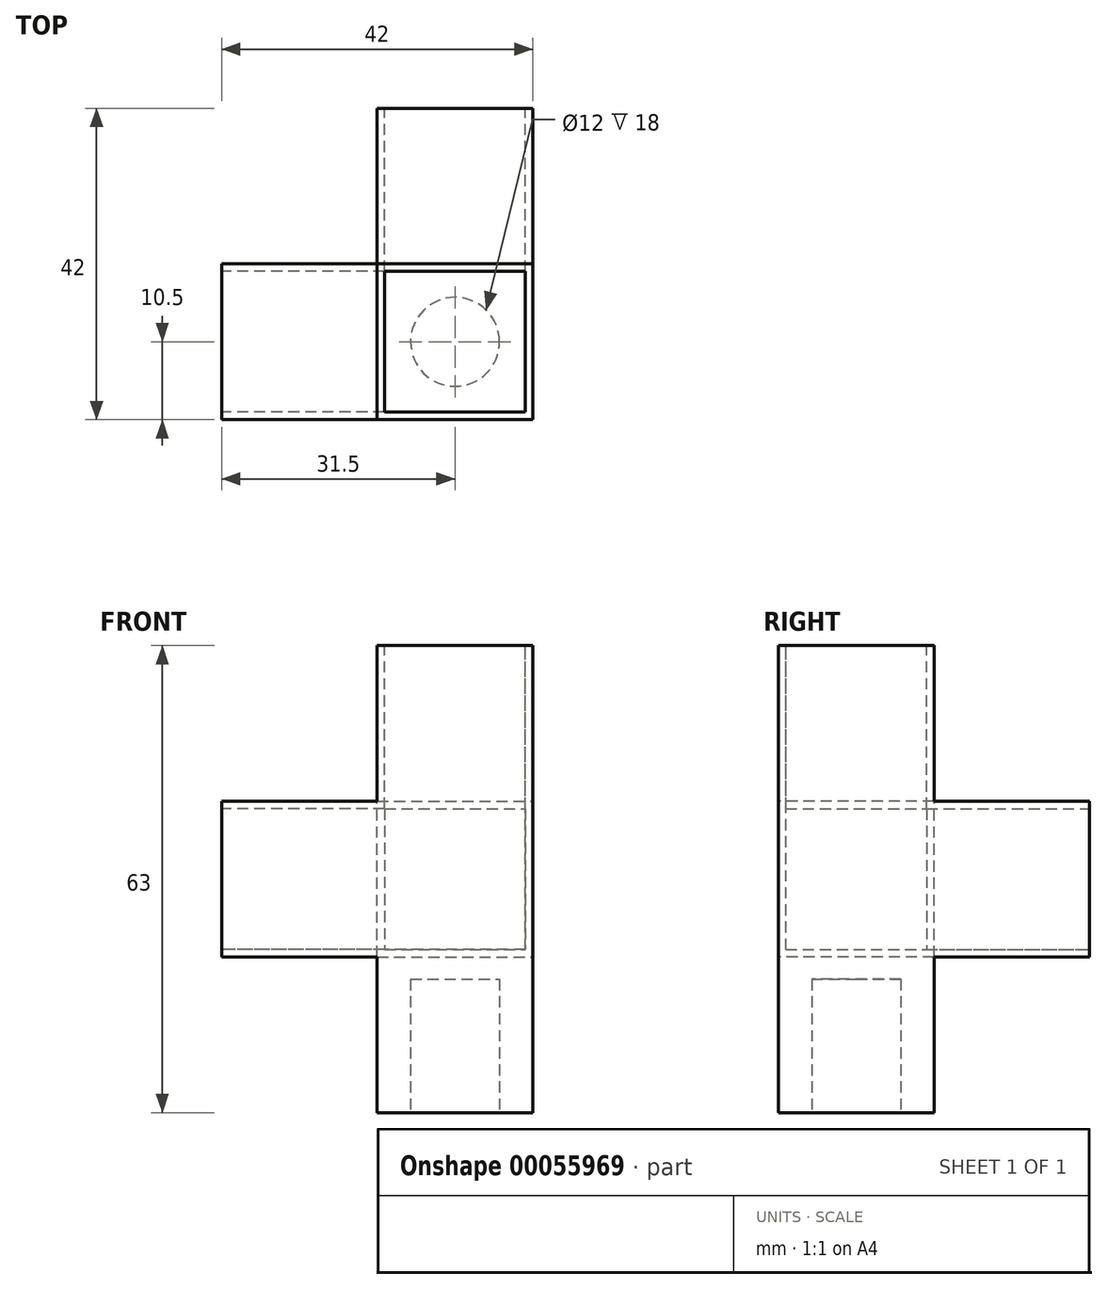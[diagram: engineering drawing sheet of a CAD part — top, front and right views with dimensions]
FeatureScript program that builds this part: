
annotation { "Feature Type Name" : "Feature", "Feature Type Description" : "" }
export const myFeature = defineFeature(function(context is Context, id is Id, definition is map)
    precondition{}
    {
        {
            var Q0;
            Q0=qCreatedBy(makeId("Top.planeOp"),FACE);
            var sketch = newSketch(context, id + "F0", { "sketchPlane" : qUnion([Q0])});
            skLineSegment(sketch, "E0.rect.bottom", {"start": v(21, 21) * mm, "end": v(-21, 21) * mm});
            skLineSegment(sketch, "E0.rect.top", {"start": v(21, -21) * mm, "end": v(-21, -21) * mm});
            skLineSegment(sketch, "E0.rect.left", {"start": v(21, 21) * mm, "end": v(21, -21) * mm});
            skLineSegment(sketch, "E0.rect.right", {"start": v(-21, 21) * mm, "end": v(-21, -21) * mm});
            skPoint(sketch, "E0.rect.middle", {"position": v(0, 0) * mm});
            skSolve(sketch);
        }
        {
            var Q0;
            Q0=makeQuery(id+"F0.imprint","IMPRINT",FACE,{"disambiguationData":[TD([[makeQuery(id+"F0.imprint","IMPRINT",EDGE,{"derivedFrom":sQuery(id+"F0.wireOp",EDGE,"E0.rect.bottom")}),1.0]])]});
            extrude(context, id + "F1", {"entities" : qUnion([Q0]), "depth" : 42 * mm});
        }
        {
            var Q0;
            Q0=makeQuery(id+"F1.opExtrude","CAP_FACE",FACE,{"disambiguationData":[OSD([sQuery(id+"F0.wireOp",EDGE,"E0.rect.bottom"),sQuery(id+"F0.wireOp",EDGE,"E0.rect.top"),sQuery(id+"F0.wireOp",EDGE,"E0.rect.left"),sQuery(id+"F0.wireOp",EDGE,"E0.rect.right")])],"isStart":false});
            var sketch = newSketch(context, id + "F2", { "sketchPlane" : qUnion([Q0])});
            skLineSegment(sketch, "E1.bottom", {"start": v(-21, 21) * mm, "end": v(0, 21) * mm});
            skLineSegment(sketch, "E1.top", {"start": v(-21, 0) * mm, "end": v(0, 0) * mm});
            skLineSegment(sketch, "E1.left", {"start": v(-21, 21) * mm, "end": v(-21, 0) * mm});
            skLineSegment(sketch, "E1.right", {"start": v(0, 21) * mm, "end": v(0, 0) * mm});
            skSolve(sketch);
        }
        {
            var Q0;
            Q0=makeQuery(id+"F2.imprint","IMPRINT",FACE,{"disambiguationData":[TD([[makeQuery(id+"F2.imprint","IMPRINT",EDGE,{"derivedFrom":sQuery(id+"F2.wireOp",EDGE,"E1.bottom")}),1.0]])]});
            extrude(context, id + "F3", {"entities" : qUnion([Q0]), "operationType" : NewBodyOperationType.REMOVE, "endBound" : BoundingType.UP_TO_NEXT, "oppositeDirection" : true, "depth" : 25 * mm});
        }
        {
            var Q0;
            Q0=makeQuery(id+"F1.opExtrude","SWEPT_FACE",FACE,{"disambiguationData":[OSD([sQuery(id+"F0.wireOp",EDGE,"E0.rect.top")])]});
            var sketch = newSketch(context, id + "F4", { "sketchPlane" : qUnion([Q0])});
            skLineSegment(sketch, "E2.bottom", {"start": v(-21, 42) * mm, "end": v(0, 42) * mm});
            skLineSegment(sketch, "E2.top", {"start": v(-21, 21) * mm, "end": v(0, 21) * mm});
            skLineSegment(sketch, "E2.left", {"start": v(-21, 42) * mm, "end": v(-21, 21) * mm});
            skLineSegment(sketch, "E2.right", {"start": v(0, 42) * mm, "end": v(0, 21) * mm});
            skSolve(sketch);
        }
        {
            var Q0;
            Q0=makeQuery(id+"F4.imprint","IMPRINT",FACE,{"disambiguationData":[TD([[makeQuery(id+"F4.imprint","IMPRINT",EDGE,{"derivedFrom":sQuery(id+"F4.wireOp",EDGE,"E2.bottom")}),1.0]])]});
            extrude(context, id + "F5", {"entities" : qUnion([Q0]), "operationType" : NewBodyOperationType.REMOVE, "endBound" : BoundingType.UP_TO_NEXT, "oppositeDirection" : true, "depth" : 25 * mm});
        }
        {
            var Q0;
            Q0=makeQuery(id+"F1.opExtrude","SWEPT_FACE",FACE,{"disambiguationData":[OSD([sQuery(id+"F0.wireOp",EDGE,"E0.rect.left")])]});
            var sketch = newSketch(context, id + "F6", { "sketchPlane" : qUnion([Q0])});
            skLineSegment(sketch, "E3.bottom", {"start": v(21, 42) * mm, "end": v(0, 42) * mm});
            skLineSegment(sketch, "E3.top", {"start": v(21, 21) * mm, "end": v(0, 21) * mm});
            skLineSegment(sketch, "E3.left", {"start": v(21, 42) * mm, "end": v(21, 21) * mm});
            skLineSegment(sketch, "E3.right", {"start": v(0, 42) * mm, "end": v(0, 21) * mm});
            skSolve(sketch);
        }
        {
            var Q0;
            Q0=makeQuery(id+"F6.imprint","IMPRINT",FACE,{"disambiguationData":[TD([[makeQuery(id+"F6.imprint","IMPRINT",EDGE,{"derivedFrom":sQuery(id+"F6.wireOp",EDGE,"E3.bottom")}),1.0]])]});
            extrude(context, id + "F7", {"entities" : qUnion([Q0]), "operationType" : NewBodyOperationType.REMOVE, "endBound" : BoundingType.UP_TO_NEXT, "oppositeDirection" : true, "depth" : 25 * mm});
        }
        {
            var Q0;
            Q0=makeQuery(id+"F1.opExtrude","CAP_FACE",FACE,{"disambiguationData":[OSD([sQuery(id+"F0.wireOp",EDGE,"E0.rect.bottom"),sQuery(id+"F0.wireOp",EDGE,"E0.rect.top"),sQuery(id+"F0.wireOp",EDGE,"E0.rect.left"),sQuery(id+"F0.wireOp",EDGE,"E0.rect.right")])],"isStart":false});
            var sketch = newSketch(context, id + "F8", { "sketchPlane" : qUnion([Q0])});
            skLineSegment(sketch, "E4", {"start": v(0, -21) * mm, "end": v(21, 0) * mm, "construction": true});
            skLineSegment(sketch, "E5.rect.bottom", {"start": v(20, -20) * mm, "end": v(1, -20) * mm});
            skLineSegment(sketch, "E5.rect.top", {"start": v(20, -1) * mm, "end": v(1, -1) * mm});
            skLineSegment(sketch, "E5.rect.left", {"start": v(20, -20) * mm, "end": v(20, -1) * mm});
            skLineSegment(sketch, "E5.rect.right", {"start": v(1, -20) * mm, "end": v(1, -1) * mm});
            skPoint(sketch, "E5.rect.middle", {"position": v(10.5, -10.5) * mm});
            skSolve(sketch);
        }
        {
            var Q0;
            Q0=makeQuery(id+"F8.imprint","IMPRINT",FACE,{"disambiguationData":[TD([[makeQuery(id+"F8.imprint","IMPRINT",EDGE,{"derivedFrom":sQuery(id+"F8.wireOp",EDGE,"E5.rect.bottom")}),-1.0]])]});
            extrude(context, id + "F9", {"entities" : qUnion([Q0]), "operationType" : NewBodyOperationType.REMOVE, "oppositeDirection" : true, "depth" : 41 * mm});
        }
        {
            var Q0;
            Q0=makeQuery(id+"F1.opExtrude","SWEPT_FACE",FACE,{"disambiguationData":[OSD([sQuery(id+"F0.wireOp",EDGE,"E0.rect.right")])]});
            var sketch = newSketch(context, id + "F10", { "sketchPlane" : qUnion([Q0])});
            skLineSegment(sketch, "E6", {"start": v(0, 0) * mm, "end": v(21, 21) * mm, "construction": true});
            skLineSegment(sketch, "E7.rect.bottom", {"start": v(20, 1) * mm, "end": v(1, 1) * mm});
            skLineSegment(sketch, "E7.rect.top", {"start": v(20, 20) * mm, "end": v(1, 20) * mm});
            skLineSegment(sketch, "E7.rect.left", {"start": v(20, 1) * mm, "end": v(20, 20) * mm});
            skLineSegment(sketch, "E7.rect.right", {"start": v(1, 1) * mm, "end": v(1, 20) * mm});
            skPoint(sketch, "E7.rect.middle", {"position": v(10.5, 10.5) * mm});
            skSolve(sketch);
        }
        {
            var Q0;
            Q0=makeQuery(id+"F10.imprint","IMPRINT",FACE,{"disambiguationData":[TD([[makeQuery(id+"F10.imprint","IMPRINT",EDGE,{"derivedFrom":sQuery(id+"F10.wireOp",EDGE,"E7.rect.bottom")}),-1.0]])]});
            extrude(context, id + "F11", {"entities" : qUnion([Q0]), "operationType" : NewBodyOperationType.REMOVE, "oppositeDirection" : true, "depth" : 41 * mm});
        }
        {
            var Q0;
            Q0=makeQuery(id+"F1.opExtrude","SWEPT_FACE",FACE,{"disambiguationData":[OSD([sQuery(id+"F0.wireOp",EDGE,"E0.rect.bottom")])]});
            var sketch = newSketch(context, id + "F12", { "sketchPlane" : qUnion([Q0])});
            skLineSegment(sketch, "E8", {"start": v(-21, 21) * mm, "end": v(0, 0) * mm, "construction": true});
            skLineSegment(sketch, "E9.rect.bottom", {"start": v(-1, 20) * mm, "end": v(-20, 20) * mm});
            skLineSegment(sketch, "E9.rect.top", {"start": v(-1, 1) * mm, "end": v(-20, 1) * mm});
            skLineSegment(sketch, "E9.rect.left", {"start": v(-1, 20) * mm, "end": v(-1, 1) * mm});
            skLineSegment(sketch, "E9.rect.right", {"start": v(-20, 20) * mm, "end": v(-20, 1) * mm});
            skPoint(sketch, "E9.rect.middle", {"position": v(-10.5, 10.5) * mm});
            skSolve(sketch);
        }
        {
            var Q0;
            Q0=makeQuery(id+"F12.imprint","IMPRINT",FACE,{"disambiguationData":[TD([[makeQuery(id+"F12.imprint","IMPRINT",EDGE,{"derivedFrom":sQuery(id+"F12.wireOp",EDGE,"E9.rect.bottom")}),1.0]])]});
            extrude(context, id + "F13", {"entities" : qUnion([Q0]), "operationType" : NewBodyOperationType.REMOVE, "oppositeDirection" : true, "depth" : 41 * mm});
        }
        {
            var Q0;
            Q0=makeQuery(id+"F1.opExtrude","CAP_FACE",FACE,{"disambiguationData":[OSD([sQuery(id+"F0.wireOp",EDGE,"E0.rect.bottom"),sQuery(id+"F0.wireOp",EDGE,"E0.rect.top"),sQuery(id+"F0.wireOp",EDGE,"E0.rect.left"),sQuery(id+"F0.wireOp",EDGE,"E0.rect.right")])],"isStart":true});
            var sketch = newSketch(context, id + "F14", { "sketchPlane" : qUnion([Q0])});
            skLineSegment(sketch, "E10.bottom", {"start": v(0, 0) * mm, "end": v(21, 0) * mm});
            skLineSegment(sketch, "E10.top", {"start": v(0, 21) * mm, "end": v(21, 21) * mm});
            skLineSegment(sketch, "E10.left", {"start": v(0, 0) * mm, "end": v(0, 21) * mm});
            skLineSegment(sketch, "E10.right", {"start": v(21, 0) * mm, "end": v(21, 21) * mm});
            skSolve(sketch);
        }
        {
            var Q0;
            Q0=makeQuery(id+"F14.imprint","IMPRINT",FACE,{"disambiguationData":[TD([[makeQuery(id+"F14.imprint","IMPRINT",EDGE,{"derivedFrom":sQuery(id+"F14.wireOp",EDGE,"E10.bottom")}),1.0]])]});
            extrude(context, id + "F15", {"entities" : qUnion([Q0]), "operationType" : NewBodyOperationType.ADD, "depth" : 21 * mm});
        }
        {
            var Q0;
            Q0=makeQuery(id+"F15.opExtrude","CAP_FACE",FACE,{"disambiguationData":[OSD([sQuery(id+"F14.wireOp",EDGE,"E10.bottom"),sQuery(id+"F14.wireOp",EDGE,"E10.top"),sQuery(id+"F14.wireOp",EDGE,"E10.left"),sQuery(id+"F14.wireOp",EDGE,"E10.right")])],"isStart":false});
            var sketch = newSketch(context, id + "F16", { "sketchPlane" : qUnion([Q0])});
            skLineSegment(sketch, "E11", {"start": v(0, 0) * mm, "end": v(21, 21) * mm, "construction": true});
            skCircle(sketch, "E12", {"center": v(10.5, 10.5) * mm, "radius": 6 * mm});
            skSolve(sketch);
        }
        {
            var Q0;
            Q0=makeQuery(id+"F16.imprint","IMPRINT",FACE,{"disambiguationData":[TD([[makeQuery(id+"F16.imprint","IMPRINT",EDGE,{"derivedFrom":sQuery(id+"F16.wireOp",EDGE,"E12")}),1.0]])]});
            extrude(context, id + "F17", {"entities" : qUnion([Q0]), "operationType" : NewBodyOperationType.REMOVE, "oppositeDirection" : true, "depth" : 18 * mm});
        }
    });
